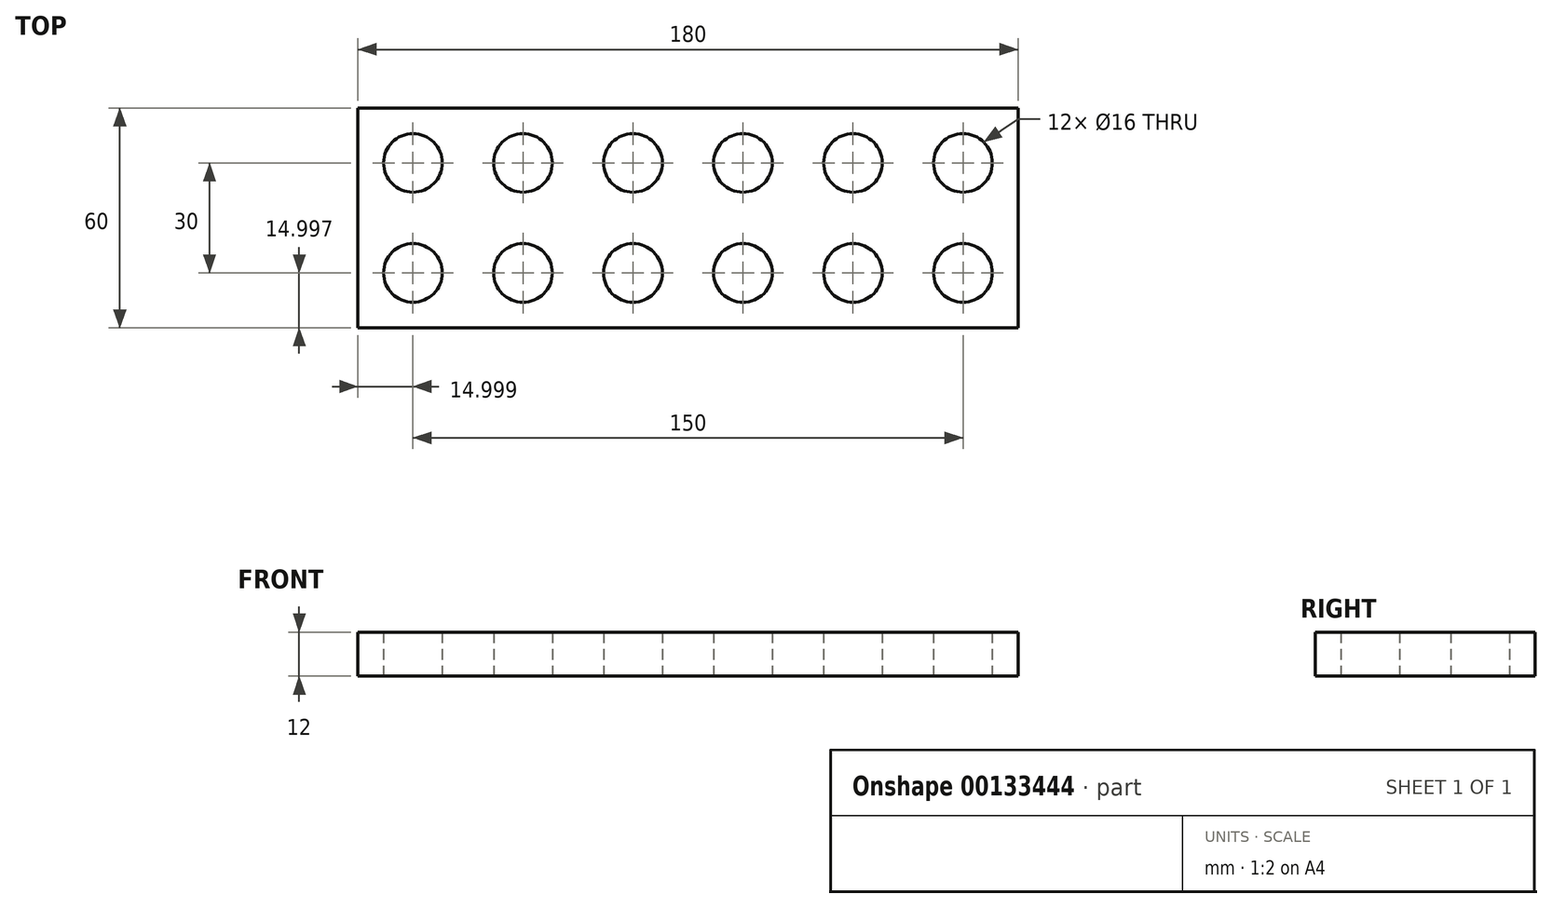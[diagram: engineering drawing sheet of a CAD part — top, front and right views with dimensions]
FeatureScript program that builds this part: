
annotation { "Feature Type Name" : "Feature", "Feature Type Description" : "" }
export const myFeature = defineFeature(function(context is Context, id is Id, definition is map)
    precondition{}
    {
        {
            var Q0;
            Q0=qCreatedBy(makeId("Top.planeOp"),FACE);
            var sketch = newSketch(context, id + "F0", { "sketchPlane" : qUnion([Q0])});
            skLineSegment(sketch, "E0.bottom", {"start": v(-78.9, 0.25) * mm, "end": v(101.1, 0.25) * mm});
            skLineSegment(sketch, "E0.top", {"start": v(-78.9, -59.75) * mm, "end": v(101.1, -59.75) * mm});
            skLineSegment(sketch, "E0.left", {"start": v(-78.9, 0.25) * mm, "end": v(-78.9, -59.75) * mm});
            skLineSegment(sketch, "E0.right", {"start": v(101.1, 0.25) * mm, "end": v(101.1, -59.75) * mm});
            skCircle(sketch, "E1", {"center": v(-63.9, -44.75) * mm, "radius": 8 * mm});
            skCircle(sketch, "E2.0.1.0", {"center": v(-63.9, -14.75) * mm, "radius": 8 * mm});
            skCircle(sketch, "E2.1.0.0", {"center": v(-33.9, -44.75) * mm, "radius": 8 * mm});
            skCircle(sketch, "E2.1.1.0", {"center": v(-33.9, -14.75) * mm, "radius": 8 * mm});
            skCircle(sketch, "E2.2.0.0", {"center": v(-3.9, -44.75) * mm, "radius": 8 * mm});
            skCircle(sketch, "E2.2.1.0", {"center": v(-3.9, -14.75) * mm, "radius": 8 * mm});
            skCircle(sketch, "E2.3.0.0", {"center": v(26.1, -44.75) * mm, "radius": 8 * mm});
            skCircle(sketch, "E2.3.1.0", {"center": v(26.1, -14.75) * mm, "radius": 8 * mm});
            skCircle(sketch, "E2.4.0.0", {"center": v(56.1, -44.75) * mm, "radius": 8 * mm});
            skCircle(sketch, "E2.4.1.0", {"center": v(56.1, -14.75) * mm, "radius": 8 * mm});
            skCircle(sketch, "E2.5.0.0", {"center": v(86.1, -44.75) * mm, "radius": 8 * mm});
            skCircle(sketch, "E2.5.1.0", {"center": v(86.1, -14.75) * mm, "radius": 8 * mm});
            skLineSegment(sketch, "E2.direction1", {"start": v(-63.9, -44.75) * mm, "end": v(-33.9, -44.75) * mm, "construction": true});
            skLineSegment(sketch, "E2.direction2", {"start": v(-63.9, -44.75) * mm, "end": v(-63.9, -14.75) * mm, "construction": true});
            skSolve(sketch);
        }
        {
            var Q0;
            Q0=makeQuery(id+"F0.imprint","IMPRINT",FACE,{"disambiguationData":[TD([[makeQuery(id+"F0.imprint","IMPRINT",EDGE,{"derivedFrom":sQuery(id+"F0.wireOp",EDGE,"E0.bottom")}),-1.0]])]});
            extrude(context, id + "F1", {"entities" : qUnion([Q0]), "depth" : 12 * mm});
        }
    });
